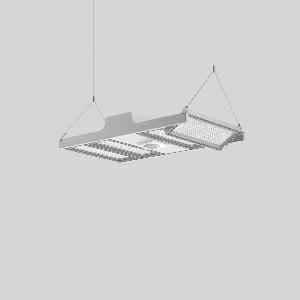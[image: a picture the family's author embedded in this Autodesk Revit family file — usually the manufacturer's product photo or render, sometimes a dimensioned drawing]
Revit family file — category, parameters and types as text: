
# Revit family: light_case_sensor_921693_004_76_d5fa
name_source: partatom
category: Lighting Fixtures
units: mm (PartAtom-declared; Revit-internal decimal feet)

## family parameters
Cut with Voids When Loaded = No
Host = Face
Light Source = No
Part Type = Normal
Room Calculation Point = No
Round Connector Dimension = Use Diameter
Shared = No

## types (1)
- LIGHT CASE SENSOR (1 x LED Modul 840, 8900 lm, 4000)
    Apparent Load = 225 VA
    CIE Flux Codes = 81 98 100 100 100
    Color Rendering = 80
    Color Temperature = 4000
    Default Elevation = 1800 mm
    Description = Series: LIGHT CASE SENSOR
Flat highbay luminaire for chain or cable suspension with 4 LED modules that can be swivelled. Housing: die cast aluminium and sheet steel, powder-coated. Optimised thermal management thanks to special luminaire design. Self-cleaning heat sink for constant heat dissipation. Cover: plastic (polycarbonate, shockproof), with integrated four-row lens system. LED modules can be swivelled ± 30° for optimum illumination. Suitable for chain or steel cable suspension (to be provided on site). With 5-pin connection terminal (1.5 m). Built-in DALI sensor for daylight- and presence-dependent lighting control. Light and presence sensor: Housing: plastic. Detection range: 12-18 m. Detection angle: to 72°. Light sensor range: 0,5-2000 lx (measured at the sensor). Installation height: 8-18 m. Example of use: Warehouses, corridors, passageways, garages. Luminaire with limited surface temperature in accordance with EN 60598-2-24 for use in environments in which a deposit of conductive dust on the luminaire can be expected. 
Colour: silver, matt (approx. RAL 9006)
Length: 680 mm
Width: 397 mm
Height: 131 mm
Lamp: LED
Socket: without socket
Colour temperature: 4000K
Colour rendering index (CRI): 80
System power: 225 W
Rated luminous flux: 35600 lm
Luminous efficiency: 158 lm/W
Control gear: Converter, dimmable, DALI
Protection class: I
Type of protection: IP 65
    Height = 131 mm
    Lamp = 1 x LED Modul 840
    Lamp Light Flux = 8900 lm
    Lamp count = 1
    Length = 680 mm
    Lifetime = 50000 h
    Luminous efficacy = 158 lm/W
    Manufacturer = RZB
    ModVariant = No
    Model = 921693.004.76
    Mounting Place = Ceiling
    Mounting Type = Pendant
    Number of Poles = 1
    OnlyDefault = Yes
    Power Factor = 1
    Product Name = LIGHT CASE SENSOR
    Product group = Pendant commercial luminaires
    ProductGroupID = 903
    Protection Class = Protection class I
    Protection Degree = IP 65
    RLX_Detail_Level = 1
    RLX_Emergency_Light_Flux = 0 lm
    RLX_Emergency_Type = 0
    RLX_Emergency_Type_DB = No
    RlxData = <blob elided: 28249 chars, md5=01cd9c55>
    Socket = socket
    Standby Power = 0 W
    System Light Flux = 35600 lm
    System Power = 225 W
    Type Comments = Product without accessories
    Type Image = 921529.004.76.jpg
    URL = http://relux.com
    VarID = ---
    Voltage = 230 V
    Voltage Range = 220-240 V
    Weight = 0.00 kg
    Width = 397 mm

## geometry (parser evidence)
native form markers: Blend x4, Sweep x20
no freeform markers — native parametric forms only
